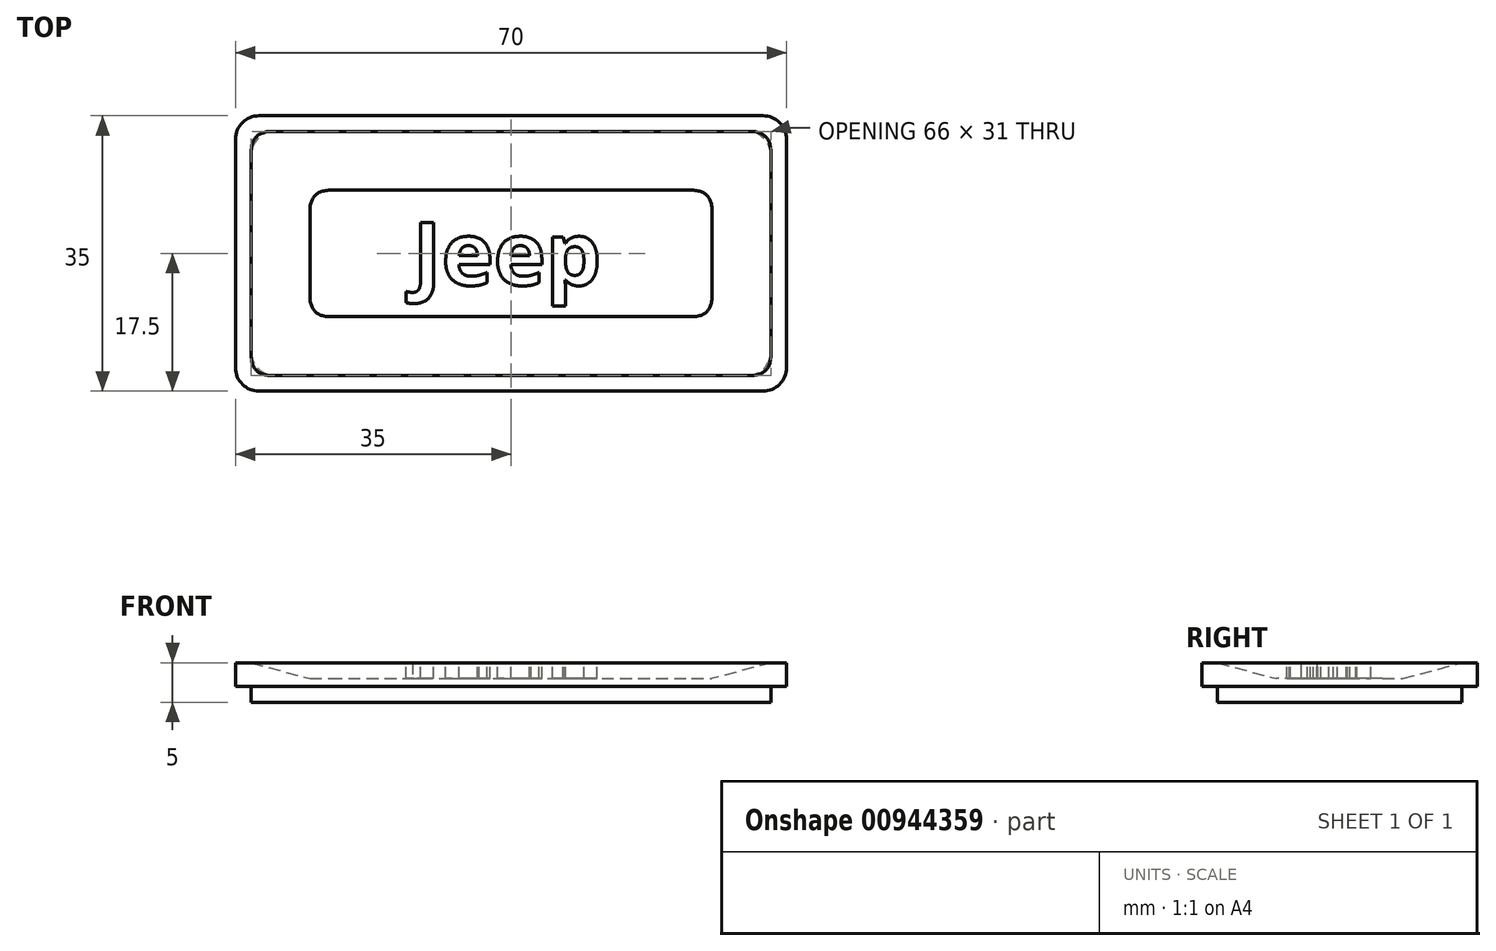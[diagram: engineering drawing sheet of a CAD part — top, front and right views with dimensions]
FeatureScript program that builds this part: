
annotation { "Feature Type Name" : "Feature", "Feature Type Description" : "" }
export const myFeature = defineFeature(function(context is Context, id is Id, definition is map)
    precondition{}
    {
        {
            var Q0;
            Q0=qCreatedBy(makeId("Top.planeOp"),FACE);
            var sketch = newSketch(context, id + "F0", { "sketchPlane" : qUnion([Q0])});
            skLineSegment(sketch, "E0.bottom", {"start": v(32, -17.5) * mm, "end": v(-32, -17.5) * mm});
            skLineSegment(sketch, "E0.top", {"start": v(32, 17.5) * mm, "end": v(-32, 17.5) * mm});
            skLineSegment(sketch, "E0.left", {"start": v(35, -14.5) * mm, "end": v(35, 14.5) * mm});
            skLineSegment(sketch, "E0.right", {"start": v(-35, -14.5) * mm, "end": v(-35, 14.5) * mm});
            skPoint(sketch, "E0.middle", {"position": v(0, 0) * mm});
            skPoint(sketch, "E1.visualSharp", {"position": v(35, 17.5) * mm});
            skArc(sketch, "E1.filletArc", {"start": v(35, 14.5) * mm, "mid": v(34.12, 16.62) * mm, "end": v(32, 17.5) * mm});
            skPoint(sketch, "E2.visualSharp", {"position": v(35, -17.5) * mm});
            skArc(sketch, "E2.filletArc", {"start": v(32, -17.5) * mm, "mid": v(34.12, -16.62) * mm, "end": v(35, -14.5) * mm});
            skPoint(sketch, "E3.visualSharp", {"position": v(-35, -17.5) * mm});
            skArc(sketch, "E3.filletArc", {"start": v(-35, -14.5) * mm, "mid": v(-34.12, -16.62) * mm, "end": v(-32, -17.5) * mm});
            skPoint(sketch, "E4.visualSharp", {"position": v(-35, 17.5) * mm});
            skArc(sketch, "E4.filletArc", {"start": v(-32, 17.5) * mm, "mid": v(-34.12, 16.62) * mm, "end": v(-35, 14.5) * mm});
            skSolve(sketch);
        }
        {
            var Q0;
            Q0 = qSketchRegion(id + "F0", true);
            extrude(context, id + "F1", {"entities" : qUnion([Q0]), "depth" : 3 * mm, "offsetDistance" : 25 * mm});
        }
        {
            var Q0;
            Q0=makeQuery(id+"F1.opExtrude","CAP_FACE",FACE,{"disambiguationData":[OSD([sQuery(id+"F0.wireOp",EDGE,"E0.bottom"),sQuery(id+"F0.wireOp",EDGE,"E0.top"),sQuery(id+"F0.wireOp",EDGE,"E0.left"),sQuery(id+"F0.wireOp",EDGE,"E0.right"),sQuery(id+"F0.wireOp",EDGE,"E1.filletArc"),sQuery(id+"F0.wireOp",EDGE,"E2.filletArc"),sQuery(id+"F0.wireOp",EDGE,"E3.filletArc"),sQuery(id+"F0.wireOp",EDGE,"E4.filletArc")])],"isStart":false});
            var sketch = newSketch(context, id + "F2", { "sketchPlane" : qUnion([Q0])});
            skLineSegment(sketch, "E5.0", {"start": v(30, -15.5) * mm, "end": v(-30, -15.5) * mm});
            skLineSegment(sketch, "E5.1", {"start": v(33, -12.5) * mm, "end": v(33, 12.5) * mm});
            skLineSegment(sketch, "E5.2", {"start": v(30, 15.5) * mm, "end": v(-30, 15.5) * mm});
            skLineSegment(sketch, "E5.3", {"start": v(-33, -12.5) * mm, "end": v(-33, 12.5) * mm});
            skPoint(sketch, "E6.visualSharp", {"position": v(33, 15.5) * mm});
            skArc(sketch, "E6.filletArc", {"start": v(33, 12.5) * mm, "mid": v(32.12, 14.62) * mm, "end": v(30, 15.5) * mm});
            skPoint(sketch, "E7.visualSharp", {"position": v(33, -15.5) * mm});
            skArc(sketch, "E7.filletArc", {"start": v(30, -15.5) * mm, "mid": v(32.12, -14.62) * mm, "end": v(33, -12.5) * mm});
            skPoint(sketch, "E8.visualSharp", {"position": v(-33, -15.5) * mm});
            skArc(sketch, "E8.filletArc", {"start": v(-33, -12.5) * mm, "mid": v(-32.12, -14.62) * mm, "end": v(-30, -15.5) * mm});
            skPoint(sketch, "E9.visualSharp", {"position": v(-33, 15.5) * mm});
            skArc(sketch, "E9.filletArc", {"start": v(-30, 15.5) * mm, "mid": v(-32.12, 14.62) * mm, "end": v(-33, 12.5) * mm});
            skSolve(sketch);
        }
        {
            var Q0;
            Q0 = qSketchRegion(id + "F2", true);
            extrude(context, id + "F3", {"entities" : qUnion([Q0]), "operationType" : NewBodyOperationType.ADD, "oppositeDirection" : true, "depth" : 5 * mm, "offsetDistance" : 25 * mm});
        }
        {
            var Q0;
            Q0=makeQuery(id+"F2.imprint","IMPRINT",FACE,{"disambiguationData":[TD([[makeQuery(id+"F2.imprint","IMPRINT",EDGE,{"derivedFrom":sQuery(id+"F2.wireOp",EDGE,"E5.0")}),-1.0]])]});
            var sketch = newSketch(context, id + "F4", { "sketchPlane" : qUnion([Q0])});
            skLineSegment(sketch, "E10.0", {"start": v(33, -15.5) * mm, "end": v(-33, -15.5) * mm});
            skLineSegment(sketch, "E10.1", {"start": v(33, -15.5) * mm, "end": v(33, 15.5) * mm});
            skLineSegment(sketch, "E10.2", {"start": v(33, 15.5) * mm, "end": v(-33, 15.5) * mm});
            skLineSegment(sketch, "E10.3", {"start": v(-33, -15.5) * mm, "end": v(-33, 15.5) * mm});
            skSolve(sketch);
        }
        {
            var Q0;
            Q0 = qSketchRegion(id + "F4", true);
            extrude(context, id + "F5", {"entities" : qUnion([Q0]), "operationType" : NewBodyOperationType.REMOVE, "oppositeDirection" : true, "depth" : 2 * mm, "offsetDistance" : 25 * mm, "hasDraft" : true, "draftAngle" : 75 * degree, "draftPullDirection" : true});
        }
        {
            var Q0;
            Q0=makeQuery(id+"F5.boolean.opBoolean","COPY",EDGE,{"derivedFrom":makeQuery(id+"F5.opExtrude","SWEPT_EDGE",EDGE,{"disambiguationData":[OSD([sQuery(id+"F4.wireOp",EDGE,"E10.2"),sQuery(id+"F4.wireOp",EDGE,"E10.3")])]})});
            var Q1;
            Q1=makeQuery(id+"F5.boolean.opBoolean","COPY",EDGE,{"derivedFrom":makeQuery(id+"F5.opExtrude","SWEPT_EDGE",EDGE,{"disambiguationData":[OSD([sQuery(id+"F4.wireOp",EDGE,"E10.1"),sQuery(id+"F4.wireOp",EDGE,"E10.2")])]})});
            var Q2;
            Q2=makeQuery(id+"F5.boolean.opBoolean","COPY",EDGE,{"derivedFrom":makeQuery(id+"F5.opExtrude","SWEPT_EDGE",EDGE,{"disambiguationData":[OSD([sQuery(id+"F4.wireOp",EDGE,"E10.0"),sQuery(id+"F4.wireOp",EDGE,"E10.1")])]})});
            var Q3;
            Q3=makeQuery(id+"F5.boolean.opBoolean","COPY",EDGE,{"derivedFrom":makeQuery(id+"F5.opExtrude","SWEPT_EDGE",EDGE,{"disambiguationData":[OSD([sQuery(id+"F4.wireOp",EDGE,"E10.0"),sQuery(id+"F4.wireOp",EDGE,"E10.3")])]})});
            fillet(context, id + "F6", {"entities" : qUnion([Q0, Q1, Q2, Q3]), "radius" : 10 * mm, "tangentPropagation" : true, "allowEdgeOverflow" : false});
        }
        {
            var Q0;
            Q0=makeQuery(id+"F2.imprint","IMPRINT",FACE,{"disambiguationData":[TD([[makeQuery(id+"F2.imprint","IMPRINT",EDGE,{"derivedFrom":sQuery(id+"F2.wireOp",EDGE,"E5.0")}),-1.0]])]});
            var sketch = newSketch(context, id + "F7", { "sketchPlane" : qUnion([Q0])});
            skLineSegment(sketch, "E11.bottom", {"start": v(12.5, -4.02) * mm, "end": v(-12.5, -4.02) * mm, "construction": true});
            skLineSegment(sketch, "E11.top", {"start": v(12.5, 4.02) * mm, "end": v(-12.5, 4.02) * mm, "construction": true});
            skLineSegment(sketch, "E11.left", {"start": v(12.5, -4.02) * mm, "end": v(12.5, 4.02) * mm, "construction": true});
            skLineSegment(sketch, "E11.right", {"start": v(-12.5, -4.02) * mm, "end": v(-12.5, 4.02) * mm, "construction": true});
            skPoint(sketch, "E11.middle", {"position": v(0, 0) * mm});
            skText(sketch, "E12", { "text": "Jeep", "fontName": "OpenSans-Bold.ttf"});
            const initialGuessF7  = {"E12": [-0.0125, -0.00402, 1, 0, 0.00804]};
            skSetInitialGuess(sketch, initialGuessF7);
            skSolve(sketch);
        }
        {
            var Q0;
            Q0 = qSketchRegion(id + "F7", true);
            extrude(context, id + "F8", {"entities" : qUnion([Q0]), "operationType" : NewBodyOperationType.ADD, "oppositeDirection" : true, "depth" : 3 * mm, "offsetDistance" : 25 * mm});
        }
    });
